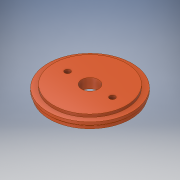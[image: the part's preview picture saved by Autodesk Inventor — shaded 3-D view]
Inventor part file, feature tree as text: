
AUTODESK INVENTOR PART (.ipt)
format: ipt  version: 2017 SP1 (Build 210196100, 196)  size: 146,944 bytes
history: native  units: in
note: dims shown in document units (in); Inventor stores cm internally (conversion verified against a paired STEP export)
features: extrude x5, sketch x5
ambient origin geometry x8: Origin, YZ Plane, XZ Plane, XY Plane, X Axis, Y Axis, Z Axis, Center Point
bodies: Solid1 (feature_tree)
feature tree (10):
  extrude  "Extrusion1"  Depth=0.25in TaperAngle=0.0deg
  extrude  "Extrusion2"  Depth=0.125in TaperAngle=0.0deg
  extrude  "Extrusion3"  Depth=0.25in TaperAngle=0.0deg
  extrude  "Extrusion7"  Depth=0.25in TaperAngle=0.0deg
  extrude  "Extrusion8"  Depth=0.25in
  sketch  "Sketch1"  dims[d0=7.25in d1=0.25in d2=0.0in]
  sketch  "Sketch2"  dims[d3=7.0in d4=0.125in d5=0.0in]
  sketch  "Sketch3"  dims[d6=7.5in d7=0.25in d8=0.0in]
  sketch  "Sketch6"  dims[d23=6.5in d24=0.25in d25=0.0in]
  sketch  "Sketch7"  dims[d27=1.5in d28=2.0in d29=2.0in d30=0.5in d31=0.25in d32=0.0in]
